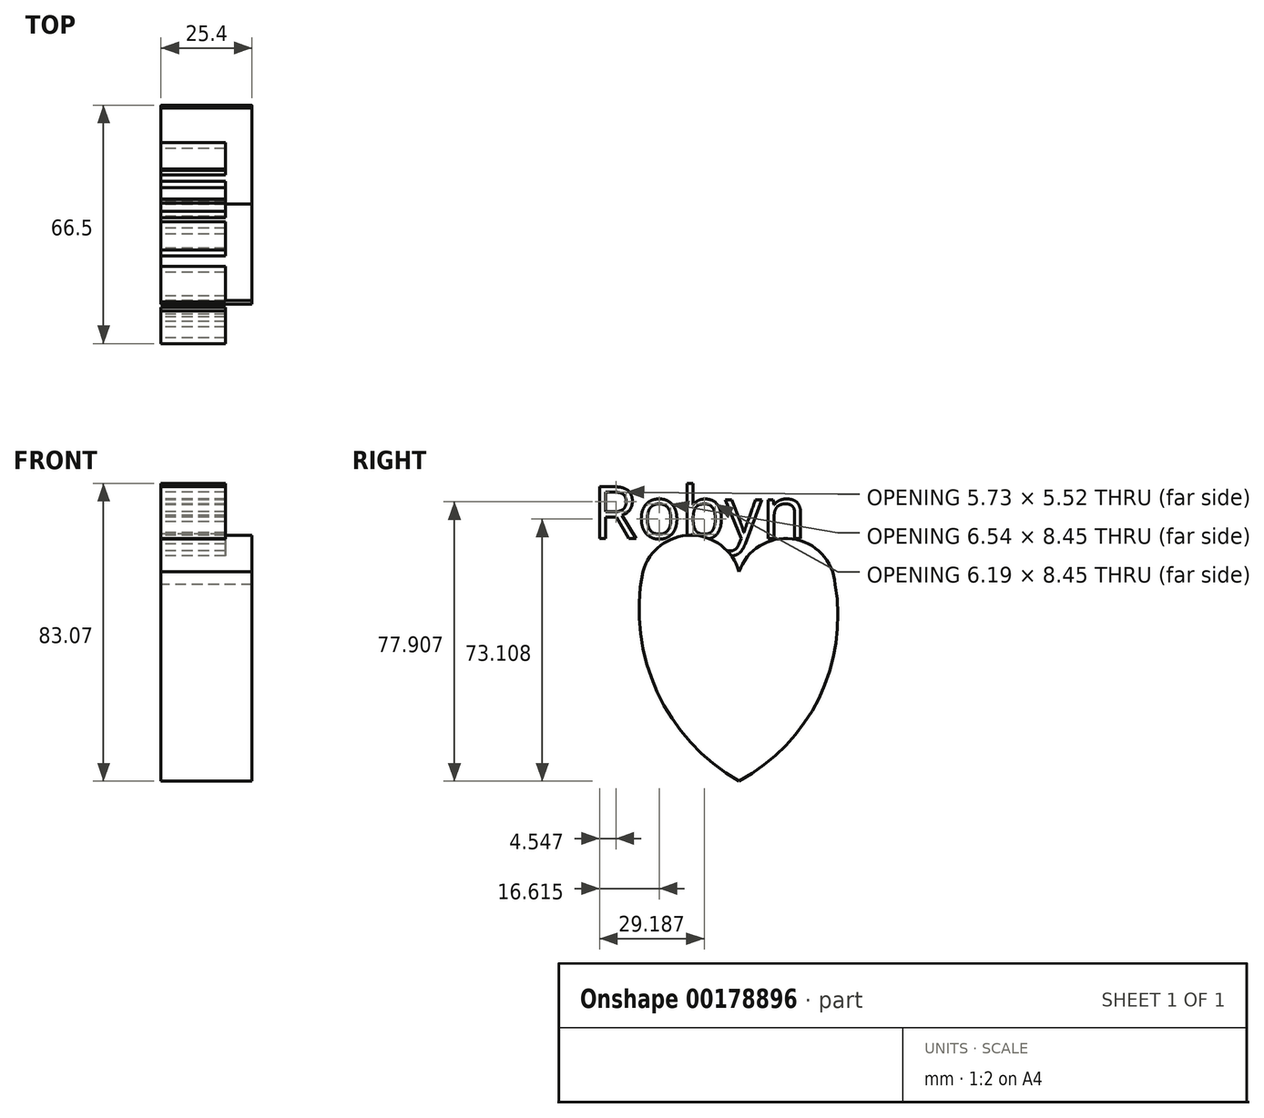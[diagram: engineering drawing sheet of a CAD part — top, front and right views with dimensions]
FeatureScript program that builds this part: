
annotation { "Feature Type Name" : "Feature", "Feature Type Description" : "" }
export const myFeature = defineFeature(function(context is Context, id is Id, definition is map)
    precondition{}
    {
        {
            var Q0;
            Q0=qCreatedBy(makeId("Right.planeOp"),FACE);
            var sketch = newSketch(context, id + "F0", { "sketchPlane" : qUnion([Q0])});
            skArc(sketch, "E0", {"start": v(26.84, 25.5) * mm, "mid": v(14.85, 38.18) * mm, "end": v(0, 29) * mm});
            skArc(sketch, "E1", {"start": v(0, 29) * mm, "mid": v(-13.42, 39.19) * mm, "end": v(-26.84, 29) * mm});
            skArc(sketch, "E2", {"start": v(-26.84, 29) * mm, "mid": v(-22.83, -4.53) * mm, "end": v(0, -29.41) * mm});
            skArc(sketch, "E3", {"start": v(0, -29.41) * mm, "mid": v(22.29, -6.29) * mm, "end": v(26.84, 25.5) * mm});
            skSolve(sketch);
        }
        {
            var Q0;
            Q0 = qSketchRegion(id + "F0", true);
            extrude(context, id + "F1", {"entities" : qUnion([Q0]), "depth" : 25.4 * mm});
        }
        {
            var Q0;
            Q0=qCreatedBy(makeId("Right.planeOp"),FACE);
            var sketch = newSketch(context, id + "F2", { "sketchPlane" : qUnion([Q0])});
            skText(sketch, "E4", { "text": "Robyn", "fontName": "OpenSans-Regular.ttf"});
            const initialGuessF2  = {"E4": [-0.04088, 0.0383, 1, 0, 0.01455]};
            skSetInitialGuess(sketch, initialGuessF2);
            skSolve(sketch);
        }
        {
            var Q0;
            Q0 = qSketchRegion(id + "F2", true);
            extrude(context, id + "F3", {"entities" : qUnion([Q0]), "operationType" : NewBodyOperationType.ADD, "depth" : 18 * mm});
        }
    });
